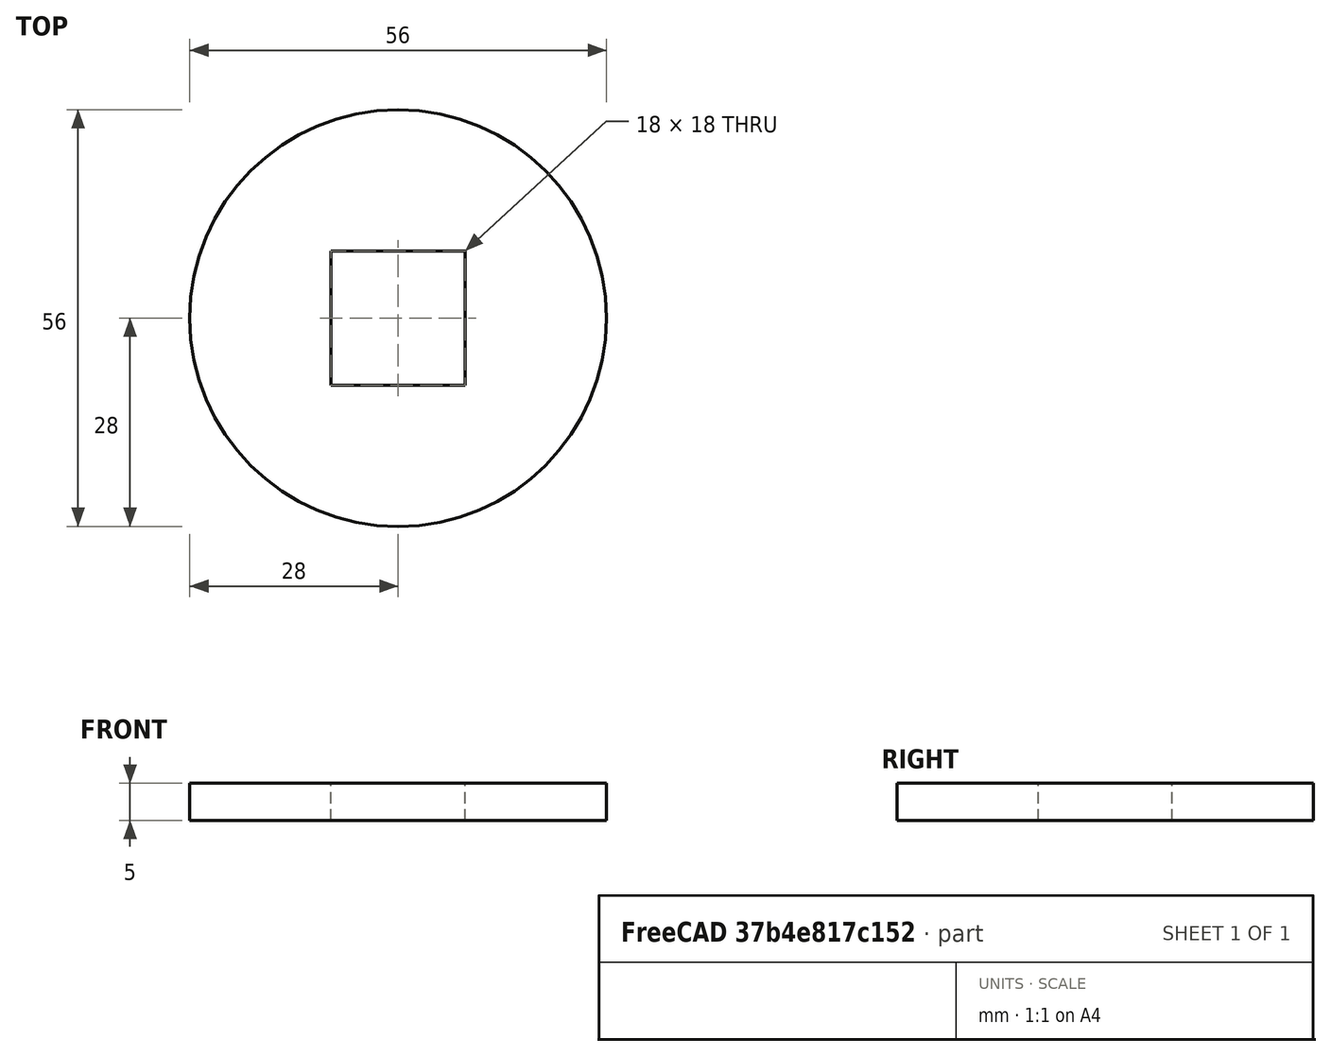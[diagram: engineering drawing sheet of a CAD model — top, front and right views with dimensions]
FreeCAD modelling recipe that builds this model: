
FCSTD DOCUMENT  (FreeCAD 0.15R4671 (Git))
Label: DIN440_CLASS_V_M16
License: CreativeCommons Attribution-ShareAlike
LicenseURL: http://creativecommons.org/licenses/by-sa/4.0/
objects: Sketcher::SketchObject×1, PartDesign::Pad×1
note: 3 computed .brp shape members not serialized (recipe doc carries the construction recipe); baked Part::Feature solids carry a one-line shape summary decoded from their .brp

FEATURE [Sketcher::SketchObject] Sketch
  sketch-geometry (5):
    g0: Circle CenterX=0 CenterY=0 CenterZ=0 NormalX=0 NormalY=0 NormalZ=1 Radius=28
    g1: LineSegment StartX=-9 StartY=9 StartZ=0 EndX=9 EndY=9 EndZ=0
    g2: LineSegment StartX=9 StartY=9 StartZ=0 EndX=9 EndY=-9 EndZ=0
    g3: LineSegment StartX=9 StartY=-9 StartZ=0 EndX=-9 EndY=-9 EndZ=0
    g4: LineSegment StartX=-9 StartY=-9 StartZ=0 EndX=-9 EndY=9 EndZ=0
  constraints (15):
    c: Coincident(g0,g-1)
    c: Radius(g0) = 28
    c: Coincident(g1,g2)
    c: Coincident(g2,g3)
    c: Coincident(g3,g4)
    c: Coincident(g4,g1)
    c: Horizontal(g1)
    c: Horizontal(g3)
    c: Vertical(g2)
    c: Vertical(g4)
    c: Equal(g1,g4)
    c: Equal(g4,g3)
    c: Equal(g3,g2)
    c: DistanceX(g1,g1) = 18
    c: Symmetric(g2,g1,g-1)
FEATURE [PartDesign::Pad] Pad
  Length = 5
  Length2 = 100
  Sketch = -> Sketch
  Type = 0
